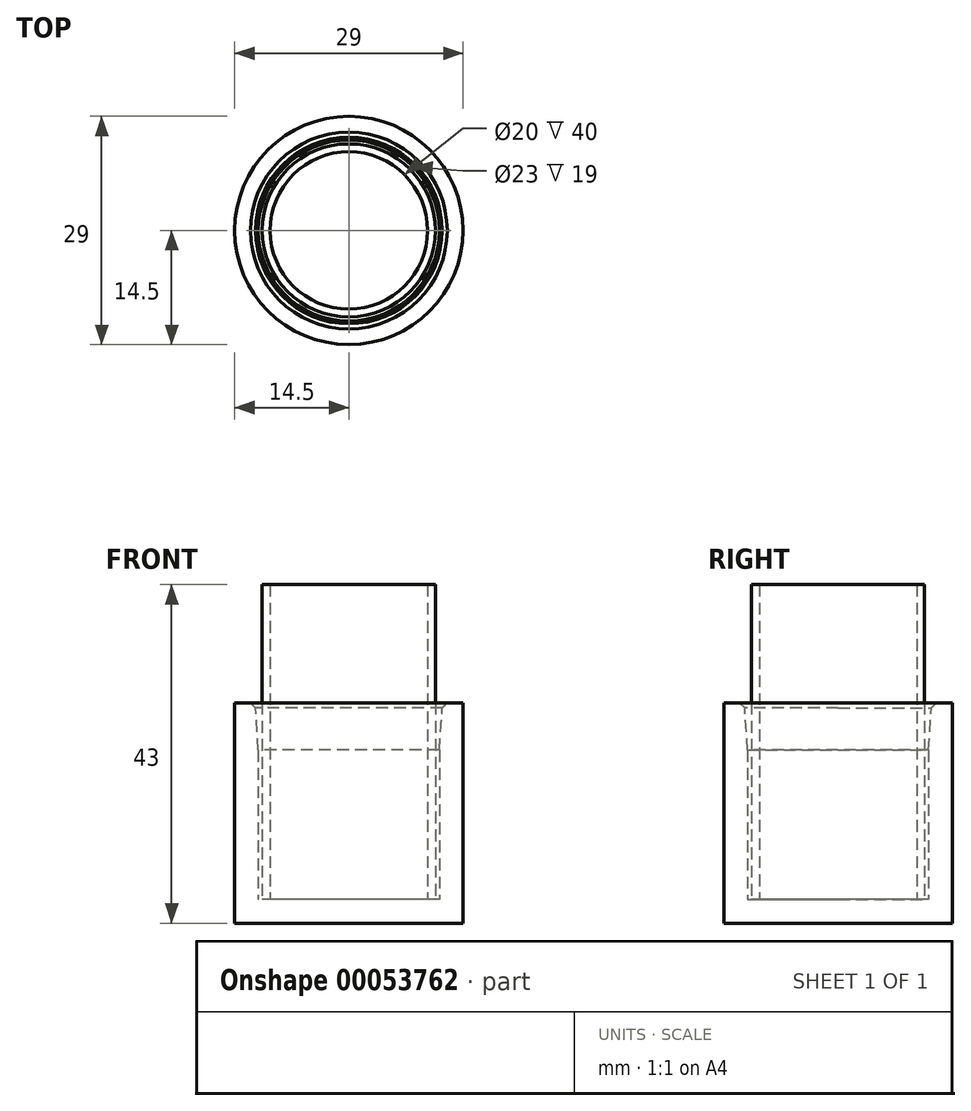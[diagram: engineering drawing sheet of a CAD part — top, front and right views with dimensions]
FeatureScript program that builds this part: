
annotation { "Feature Type Name" : "Feature", "Feature Type Description" : "" }
export const myFeature = defineFeature(function(context is Context, id is Id, definition is map)
    precondition{}
    {
        {
            var Q0;
            Q0=qCreatedBy(makeId("Top.planeOp"),FACE);
            var sketch = newSketch(context, id + "F0", { "sketchPlane" : qUnion([Q0])});
            skCircle(sketch, "E0", {"center": v(0, 0) * mm, "radius": 10 * mm});
            skCircle(sketch, "E1.0", {"center": v(0, 0) * mm, "radius": 11 * mm});
            skSolve(sketch);
        }
        {
            var Q0;
            Q0 = qSketchRegion(id + "F0", true);
            extrude(context, id + "F1", {"entities" : qUnion([Q0]), "depth" : 40 * mm});
        }
        {
            var Q0;
            Q0=qCreatedBy(makeId("Top.planeOp"),FACE);
            var sketch = newSketch(context, id + "F2", { "sketchPlane" : qUnion([Q0])});
            skCircle(sketch, "E2.0", {"center": v(0, 0) * mm, "radius": 11 * mm});
            skCircle(sketch, "E3.0", {"center": v(0, 0) * mm, "radius": 11.5 * mm});
            skCircle(sketch, "E4.0", {"center": v(0, 0) * mm, "radius": 14.5 * mm});
            skSolve(sketch);
        }
        {
            var Q0;
            Q0 = qSketchRegion(id + "F2", true);
            extrude(context, id + "F3", {"entities" : qUnion([Q0]), "depth" : 25 * mm});
        }
        {
            var Q0;
            Q0=qCreatedBy(makeId("Top.planeOp"),FACE);
            var sketch = newSketch(context, id + "F4", { "sketchPlane" : qUnion([Q0])});
            skCircle(sketch, "E5.0", {"center": v(0, 0) * mm, "radius": 14.5 * mm});
            skSolve(sketch);
        }
        {
            var Q0;
            Q0 = qSketchRegion(id + "F4", true);
            extrude(context, id + "F5", {"entities" : qUnion([Q0]), "operationType" : NewBodyOperationType.ADD, "oppositeDirection" : true, "depth" : 3 * mm});
        }
        {
            var Q0;
            Q0=makeQuery(id+"F3.opExtrude","CAP_EDGE",EDGE,{"disambiguationData":[OSD([sQuery(id+"F2.wireOp",EDGE,"E3.0")])],"isStart":false});
            chamfer(context, id + "F6", {"entities" : qUnion([Q0]), "width" : 1 * mm, "tangentPropagation" : true});
        }
        {
            var Q0;
            {var subQ0=sQuery(id+"F2.wireOp",EDGE,"E3.0");Q0=makeQuery(id+"F6.opChamfer","BLEND_EDGE",EDGE,{"blendedFrom":[makeQuery(id+"F3.opExtrude","CAP_EDGE",EDGE,{"disambiguationData":[OSD([subQ0])],"isStart":false}),makeQuery(id+"F3.opExtrude","SWEPT_FACE",FACE,{"disambiguationData":[OSD([subQ0])]})],"blendedInto":[makeQuery(id+"F3.opExtrude","SWEPT_FACE",FACE,{"disambiguationData":[OSD([subQ0])]})]});}
            chamfer(context, id + "F7", {"entities" : qUnion([Q0]), "chamferType" : ChamferType.TWO_OFFSETS, "width1" : 0.5 * mm, "oppositeDirection" : true, "width2" : 5 * mm, "tangentPropagation" : true});
        }
    });
